# Revit family: CR001_International
name_source: partatom
category: Оборудование
revit_build: Autodesk Revit 2018 (Build: 20170223_1515(x64)
units: mm (PartAtom-declared; Revit-internal decimal feet)

## family parameters
Всегда вертикально = Нет
Заголовок OmniClass = Supply and Distribution of Liquids and Gases
На основе рабочей плоскости = Нет
Номер OmniClass = 23.65.00.00
Общий = Нет
При загрузке вырезать с полостями = Нет
Размер круглого соединителя = Использовать диаметр
Тип детали = Вставляется
Точка расчета площади = Нет

## types (1)
- CR001_International
    ADSK_Единица измерения = шт
    ADSK_Завод-изготовитель = Grundfos
    ADSK_Код изделия = 95922155
    ADSK_Марка = CR 120-5-1
    ADSK_Наименование = Вертикалные многоступенчатые центробежные насосыl
    ADSK_Расход жидкости = 0 м³/ч
    Box Material = Steel - Grundfos - Black
    Date Last Modified = August 17, 2016
    Efficiency Rating = IE3
    Enclosure Rating = 55 (Protect. water jets/dust)
    Equipment Abbreviation = PMP
    Family Version = 1.0
    Flow = 0 м³/ч
    Gross Weight = 1198.649 фунт
    Head = 59.43 фунт на квадратный дюйм
    Load Classification = Other
    Manufacturer Ar. No. = 5700838933642
    Manufacturer Website = www.grundfos.com
    Maximum Motor Power Rating = 45
    Maximum Operating Pressure = 435.11 фунт на квадратный дюйм
    Maximum Operating Temperature = 131 °F
    Model Disclaimer = Для дополнительной информации обратитесь в представительство Grundfos
    Motor Material = Steel - Grundfos - Black
    Net Weight = 0.000 фунт
    Number of Poles = 1
    OmniClass = 23.27.17.00
    Port to Port = 380 мм
    PowerFactor = 0.89
    PowerFactor Range = 0.89
    Product Model Number = 95922155
    Product Range = CRFAM
    ProductCode = CR 120-5-1
    Pump Material = Steel - Grundfos - Black
    Revit Version = 2014
    SupplyFrequency = 50 Гц
    SupplyPhase = 3
    SupplyVoltage = 400 В
    SupplyVoltage Range = 380-420D/660-725Y
    URL = http://product-selection.grundfos.com
    z B1 = 1456 мм
    z B2 = 708 мм
    z B3 = 180 мм
    z B4 = 43 мм
    z Base Corner Radius = 43 мм
    z Base Height = 43 мм
    z Base Length = 344 мм
    z Base Width = 472 мм
    z Box Width Left = 221 мм
    z Box Width Right = 221 мм
    z Column Bolt Radius = 21.5 мм
    z Column Radius = 129 мм
    z Coupler Diameter = 442 мм
    z Coupler Radius = 221 мм
    z Coupler Radius Bottom = 141.7 мм
    z Coupler Radius Top = 178 мм
    z Coupler Size Bottom = 283.4 мм
    z Coupler Size Top = 356 мм
    z D1 = 442 мм
    z D1 Corner Radius = 110.5 мм
    z D1r = 221 мм
    z D2 = 325 мм
    z D3 = 0 мм
    z D4 = 275 мм
    z D5 = 344 мм
    z D6 = 380 мм
    z D7 = 380 мм
    z D8 = 472 мм
    z Discharge Flange Radius = 62.5 мм
    z Discharge Radius = 62.5 мм
    z Discharge Size = 125 мм
    z Flange Diameter Discharge = 270 мм
    z Flange Diameter Discharge Actual = 125 мм
    z Flange Diameter Suction = 270 мм
    z Flange Diameter Suction Actual = 125 мм
    z Flange Thickness Discharge = 1 мм
    z Flange Thickness Suction = 1 мм
    z Mounting Length = 275 мм
    z Mounting Width = 380 мм
    z Nominal Diameter Discharge = 125 мм
    z Nominal Diameter Suction = 125 мм
    z Port Elevation = 180 мм
    z Port to Port Length = 380 мм
    z Pump Size = 100 мм
    z Suction Flange Radius = 62.5 мм
    z Suction Radius = 62.5 мм
    z Suction Size = 125 мм
    z Visible Flanged = Нет
    z Visible Ported = Да
    z Visible Portless = Нет
    Группа модели = CR 120-5-1
    Изготовитель = Grundfos
    Описание = Вертикалные многоступенчатые центробежные насосыl

## geometry (parser evidence)
native form markers: Sweep x4
no freeform markers — native parametric forms only
